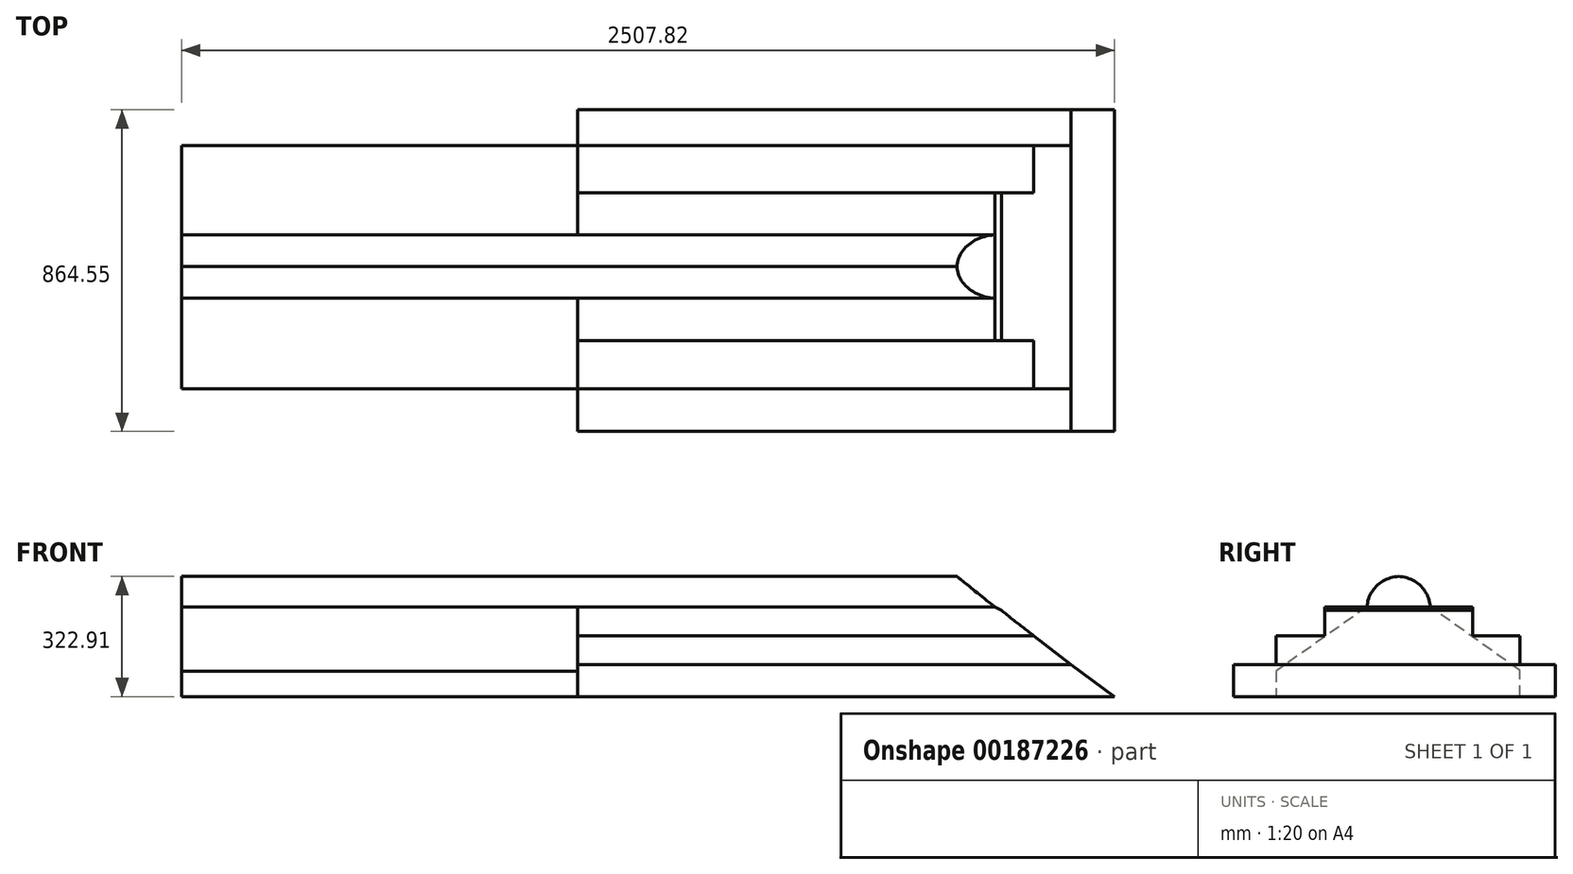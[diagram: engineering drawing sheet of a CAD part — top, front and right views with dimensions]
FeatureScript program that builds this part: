
annotation { "Feature Type Name" : "Feature", "Feature Type Description" : "" }
export const myFeature = defineFeature(function(context is Context, id is Id, definition is map)
    precondition{}
    {
        {
            var Q0;
            Q0=qCreatedBy(makeId("Front.planeOp"),FACE);
            var sketch = newSketch(context, id + "F0", { "sketchPlane" : qUnion([Q0])});
            skLineSegment(sketch, "E0", {"start": v(1047.84, -354.35) * mm, "end": v(909.4, -277.22) * mm});
            skLineSegment(sketch, "E1", {"start": v(909.4, -277.22) * mm, "end": v(-211.95, -277.22) * mm});
            skLineSegment(sketch, "E2", {"start": v(-211.95, -277.22) * mm, "end": v(-211.95, -354.35) * mm});
            skLineSegment(sketch, "E3", {"start": v(-211.95, -354.35) * mm, "end": v(1047.84, -354.35) * mm});
            skSolve(sketch);
        }
        {
            var Q0;
            Q0 = qSketchRegion(id + "F0", true);
            extrude(context, id + "F1", {"entities" : qUnion([Q0]), "oppositeDirection" : true, "depth" : 397.47 * mm});
        }
        {
            var Q0;
            Q0=makeQuery(id+"F1.opExtrude","SWEPT_FACE",FACE,{"disambiguationData":[OSD([sQuery(id+"F0.wireOp",EDGE,"E2")])]});
            var sketch = newSketch(context, id + "F2", { "sketchPlane" : qUnion([Q0])});
            skLineSegment(sketch, "E4", {"start": v(-397.47, -354.35) * mm, "end": v(-524.6, -354.35) * mm});
            skLineSegment(sketch, "E5", {"start": v(-524.6, -354.35) * mm, "end": v(-524.6, -432.67) * mm});
            skLineSegment(sketch, "E6", {"start": v(-524.6, -432.67) * mm, "end": v(130.1, -432.67) * mm});
            skLineSegment(sketch, "E7", {"start": v(130.1, -432.67) * mm, "end": v(130.1, -354.35) * mm});
            skLineSegment(sketch, "E8", {"start": v(130.1, -354.35) * mm, "end": v(0, -354.35) * mm});
            skSolve(sketch);
        }
        {
            var Q0;
            Q0=makeQuery(id+"F2.imprint","IMPRINT",FACE,{"disambiguationData":[TD([[makeQuery(id+"F2.imprint","IMPRINT",EDGE,{"derivedFrom":sQuery(id+"F2.wireOp",EDGE,"E4")}),1.0]])]});
            extrude(context, id + "F3", {"entities" : qUnion([Q0]), "operationType" : NewBodyOperationType.ADD, "oppositeDirection" : true, "depth" : 1384.37 * mm});
        }
        {
            var Q0;
            Q0=makeQuery(id+"F3.opExtrude","CAP_EDGE",EDGE,{"disambiguationData":[OSD([sQuery(id+"F0.wireOp",EDGE,"E2"),sQuery(id+"F0.wireOp",EDGE,"E3"),sQuery(id+"F2.wireOp",EDGE,"E4"),sQuery(id+"F2.wireOp",EDGE,"E8")])],"isStart":false});
            chamfer(context, id + "F4", {"entities" : qUnion([Q0]), "chamferType" : ChamferType.OFFSET_ANGLE, "width" : 124.46 * mm, "oppositeDirection" : false, "angle" : 52 * degree, "tangentPropagation" : true});
        }
        {
            var Q0;
            {var subQ0=sQuery(id+"F0.wireOp",EDGE,"E2");Q0=makeQuery(id+"F3.boolean.opBoolean","MERGE",FACE,{"derivedFrom":[makeQuery(id+"F1.opExtrude","SWEPT_FACE",FACE,{"disambiguationData":[OSD([subQ0])]}),makeQuery(id+"F3.opExtrude","CAP_FACE",FACE,{"disambiguationData":[OSD([subQ0,sQuery(id+"F0.wireOp",EDGE,"E3"),sQuery(id+"F2.wireOp",EDGE,"E4"),sQuery(id+"F2.wireOp",EDGE,"E5"),sQuery(id+"F2.wireOp",EDGE,"E6"),sQuery(id+"F2.wireOp",EDGE,"E7"),sQuery(id+"F2.wireOp",EDGE,"E8")])],"isStart":true})]});}
            var sketch = newSketch(context, id + "F5", { "sketchPlane" : qUnion([Q0])});
            skLineSegment(sketch, "E9.bottom", {"start": v(-620.44, -432.67) * mm, "end": v(244.11, -432.67) * mm});
            skLineSegment(sketch, "E9.top", {"start": v(-620.44, -518.25) * mm, "end": v(244.11, -518.25) * mm});
            skLineSegment(sketch, "E9.left", {"start": v(-620.44, -432.67) * mm, "end": v(-620.44, -518.25) * mm});
            skLineSegment(sketch, "E9.right", {"start": v(244.11, -432.67) * mm, "end": v(244.11, -518.25) * mm});
            skSolve(sketch);
        }
        {
            var Q0;
            Q0 = qSketchRegion(id + "F5", true);
            extrude(context, id + "F6", {"entities" : qUnion([Q0]), "operationType" : NewBodyOperationType.ADD, "oppositeDirection" : true, "depth" : 790.16 * mm});
        }
        {
            var Q0;
            Q0=makeQuery(id+"F6.opExtrude","CAP_FACE",FACE,{"disambiguationData":[OSD([sQuery(id+"F5.wireOp",EDGE,"E9.bottom"),sQuery(id+"F5.wireOp",EDGE,"E9.top"),sQuery(id+"F5.wireOp",EDGE,"E9.left"),sQuery(id+"F5.wireOp",EDGE,"E9.right")])],"isStart":false});
            extrude(context, id + "F7", {"entities" : qUnion([Q0]), "operationType" : NewBodyOperationType.ADD, "depth" : 613 * mm});
        }
        {
            var Q0;
            Q0=makeQuery(id+"F7.opExtrude","CAP_FACE",FACE,{"disambiguationData":[OSD([sQuery(id+"F5.wireOp",EDGE,"E9.bottom"),sQuery(id+"F5.wireOp",EDGE,"E9.top"),sQuery(id+"F5.wireOp",EDGE,"E9.left"),sQuery(id+"F5.wireOp",EDGE,"E9.right")])],"isStart":false});
            extrude(context, id + "F8", {"entities" : qUnion([Q0]), "operationType" : NewBodyOperationType.ADD, "depth" : 11.42 * mm});
        }
        {
            var Q0;
            Q0=makeQuery(id+"F8.opExtrude","CAP_FACE",FACE,{"disambiguationData":[OSD([sQuery(id+"F5.wireOp",EDGE,"E9.bottom"),sQuery(id+"F5.wireOp",EDGE,"E9.top"),sQuery(id+"F5.wireOp",EDGE,"E9.left"),sQuery(id+"F5.wireOp",EDGE,"E9.right")])],"isStart":false});
            extrude(context, id + "F9", {"entities" : qUnion([Q0]), "operationType" : NewBodyOperationType.ADD, "depth" : 29.71 * mm});
        }
        {
            var Q0;
            Q0=makeQuery(id+"F9.opExtrude","CAP_EDGE",EDGE,{"disambiguationData":[OSD([sQuery(id+"F5.wireOp",EDGE,"E9.bottom")])],"isStart":false});
            chamfer(context, id + "F10", {"entities" : qUnion([Q0]), "chamferType" : ChamferType.TWO_OFFSETS, "width1" : 86.36 * mm, "oppositeDirection" : false, "width2" : 118.11 * mm, "tangentPropagation" : true});
        }
        {
            var Q0;
            {var subQ0=sQuery(id+"F0.wireOp",EDGE,"E2");Q0=makeQuery(id+"F6.boolean.opBoolean","MERGE",FACE,{"derivedFrom":[makeQuery(id+"F3.boolean.opBoolean","MERGE",FACE,{"derivedFrom":[makeQuery(id+"F1.opExtrude","SWEPT_FACE",FACE,{"disambiguationData":[OSD([subQ0])]}),makeQuery(id+"F3.opExtrude","CAP_FACE",FACE,{"disambiguationData":[OSD([subQ0,sQuery(id+"F0.wireOp",EDGE,"E3"),sQuery(id+"F2.wireOp",EDGE,"E4"),sQuery(id+"F2.wireOp",EDGE,"E5"),sQuery(id+"F2.wireOp",EDGE,"E6"),sQuery(id+"F2.wireOp",EDGE,"E7"),sQuery(id+"F2.wireOp",EDGE,"E8")])],"isStart":true})]}),makeQuery(id+"F6.opExtrude","CAP_FACE",FACE,{"disambiguationData":[OSD([sQuery(id+"F5.wireOp",EDGE,"E9.bottom"),sQuery(id+"F5.wireOp",EDGE,"E9.top"),sQuery(id+"F5.wireOp",EDGE,"E9.left"),sQuery(id+"F5.wireOp",EDGE,"E9.right")])],"isStart":true})]});}
            var sketch = newSketch(context, id + "F11", { "sketchPlane" : qUnion([Q0])});
            skLineSegment(sketch, "E10.bottom", {"start": v(-284.6, -277.22) * mm, "end": v(-113.72, -277.22) * mm});
            skLineSegment(sketch, "E10.top", {"start": v(-284.6, -195.28) * mm, "end": v(-113.72, -195.28) * mm});
            skLineSegment(sketch, "E10.left", {"start": v(-284.6, -277.22) * mm, "end": v(-284.6, -195.28) * mm});
            skLineSegment(sketch, "E10.right", {"start": v(-113.72, -277.22) * mm, "end": v(-113.72, -195.28) * mm});
            skSolve(sketch);
        }
        {
            var Q0;
            Q0 = qSketchRegion(id + "F11", true);
            extrude(context, id + "F12", {"entities" : qUnion([Q0]), "operationType" : NewBodyOperationType.ADD, "oppositeDirection" : true, "depth" : 1120.73 * mm});
        }
        {
            var Q0;
            Q0=makeQuery(id+"F12.opExtrude","CAP_EDGE",EDGE,{"disambiguationData":[OSD([sQuery(id+"F11.wireOp",EDGE,"E10.top")])],"isStart":false});
            chamfer(context, id + "F13", {"entities" : qUnion([Q0]), "chamferType" : ChamferType.TWO_OFFSETS, "width1" : 81.8 * mm, "oppositeDirection" : false, "width2" : 101.6 * mm, "tangentPropagation" : true});
        }
        {
            var Q0;
            Q0=makeQuery(id+"F12.opExtrude","SWEPT_EDGE",EDGE,{"disambiguationData":[OSD([sQuery(id+"F11.wireOp",EDGE,"E10.top"),sQuery(id+"F11.wireOp",EDGE,"E10.left")])]});
            var Q1;
            Q1=makeQuery(id+"F12.opExtrude","SWEPT_EDGE",EDGE,{"disambiguationData":[OSD([sQuery(id+"F11.wireOp",EDGE,"E10.top"),sQuery(id+"F11.wireOp",EDGE,"E10.right")])]});
            fillet(context, id + "F14", {"entities" : qUnion([Q0, Q1]), "radius" : 88.9 * mm, "tangentPropagation" : true, "allowEdgeOverflow" : false});
        }
        {
            var Q0;
            {var subQ0=sQuery(id+"F0.wireOp",EDGE,"E2");Q0=makeQuery(id+"F12.boolean.opBoolean","MERGE",FACE,{"derivedFrom":[makeQuery(id+"F6.boolean.opBoolean","MERGE",FACE,{"derivedFrom":[makeQuery(id+"F3.boolean.opBoolean","MERGE",FACE,{"derivedFrom":[makeQuery(id+"F1.opExtrude","SWEPT_FACE",FACE,{"disambiguationData":[OSD([subQ0])]}),makeQuery(id+"F3.opExtrude","CAP_FACE",FACE,{"disambiguationData":[OSD([subQ0,sQuery(id+"F0.wireOp",EDGE,"E3"),sQuery(id+"F2.wireOp",EDGE,"E4"),sQuery(id+"F2.wireOp",EDGE,"E5"),sQuery(id+"F2.wireOp",EDGE,"E6"),sQuery(id+"F2.wireOp",EDGE,"E7"),sQuery(id+"F2.wireOp",EDGE,"E8")])],"isStart":true})]}),makeQuery(id+"F6.opExtrude","CAP_FACE",FACE,{"disambiguationData":[OSD([sQuery(id+"F5.wireOp",EDGE,"E9.bottom"),sQuery(id+"F5.wireOp",EDGE,"E9.top"),sQuery(id+"F5.wireOp",EDGE,"E9.left"),sQuery(id+"F5.wireOp",EDGE,"E9.right")])],"isStart":true})]}),makeQuery(id+"F12.opExtrude","CAP_FACE",FACE,{"disambiguationData":[OSD([sQuery(id+"F11.wireOp",EDGE,"E10.bottom"),sQuery(id+"F11.wireOp",EDGE,"E10.top"),sQuery(id+"F11.wireOp",EDGE,"E10.left"),sQuery(id+"F11.wireOp",EDGE,"E10.right")])],"isStart":true})]});}
            var sketch = newSketch(context, id + "F15", { "sketchPlane" : qUnion([Q0])});
            skLineSegment(sketch, "E11", {"start": v(-524.6, -518.25) * mm, "end": v(-524.6, -448.06) * mm});
            skLineSegment(sketch, "E12", {"start": v(-524.6, -448.06) * mm, "end": v(-284.6, -277.22) * mm});
            skLineSegment(sketch, "E13", {"start": v(-284.6, -277.22) * mm, "end": v(-113.72, -277.22) * mm});
            skLineSegment(sketch, "E14", {"start": v(-113.72, -277.22) * mm, "end": v(130.1, -449.86) * mm});
            skLineSegment(sketch, "E15", {"start": v(130.1, -449.86) * mm, "end": v(130.1, -518.25) * mm});
            skLineSegment(sketch, "E16", {"start": v(130.1, -518.25) * mm, "end": v(-524.6, -518.25) * mm});
            skSolve(sketch);
        }
        {
            var Q0;
            Q0 = qSketchRegion(id + "F15", true);
            extrude(context, id + "F16", {"entities" : qUnion([Q0]), "operationType" : NewBodyOperationType.ADD, "depth" : 1064.6 * mm});
        }
        {
            var Q0;
            Q0=makeQuery(id+"F16.opExtrude","CAP_FACE",FACE,{"disambiguationData":[OSD([sQuery(id+"F15.wireOp",EDGE,"E11"),sQuery(id+"F15.wireOp",EDGE,"E12"),sQuery(id+"F15.wireOp",EDGE,"E13"),sQuery(id+"F15.wireOp",EDGE,"E14"),sQuery(id+"F15.wireOp",EDGE,"E15"),sQuery(id+"F15.wireOp",EDGE,"E16")])],"isStart":false});
            extrude(context, id + "F17", {"entities" : qUnion([Q0]), "operationType" : NewBodyOperationType.ADD, "oppositeDirection" : true, "depth" : 77.8 * mm});
        }
        {
            var Q0;
            {var subQ0=makeQuery(id+"F6.opExtrude","CAP_FACE",FACE,{"disambiguationData":[OSD([sQuery(id+"F5.wireOp",EDGE,"E9.bottom"),sQuery(id+"F5.wireOp",EDGE,"E9.top"),sQuery(id+"F5.wireOp",EDGE,"E9.left"),sQuery(id+"F5.wireOp",EDGE,"E9.right")])],"isStart":true});var subQ1=sQuery(id+"F0.wireOp",EDGE,"E2");var subQ2=makeQuery(id+"F3.opExtrude","CAP_FACE",FACE,{"disambiguationData":[OSD([subQ1,sQuery(id+"F0.wireOp",EDGE,"E3"),sQuery(id+"F2.wireOp",EDGE,"E4"),sQuery(id+"F2.wireOp",EDGE,"E5"),sQuery(id+"F2.wireOp",EDGE,"E6"),sQuery(id+"F2.wireOp",EDGE,"E7"),sQuery(id+"F2.wireOp",EDGE,"E8")])],"isStart":true});var subQ3=makeQuery(id+"F1.opExtrude","SWEPT_FACE",FACE,{"disambiguationData":[OSD([subQ1])]});var subQ4=sQuery(id+"F11.wireOp",EDGE,"E10.right");var subQ5=sQuery(id+"F11.wireOp",EDGE,"E10.left");var subQ6=sQuery(id+"F11.wireOp",EDGE,"E10.top");var subQ7=makeQuery(id+"F12.opExtrude","CAP_FACE",FACE,{"disambiguationData":[OSD([sQuery(id+"F11.wireOp",EDGE,"E10.bottom"),subQ6,subQ5,subQ4])],"isStart":true});Q0=makeQuery(id+"F16.boolean.opBoolean","SPLIT",FACE,{"disambiguationData":[TD([makeQuery(id+"F1.opExtrude","SWEPT_FACE",FACE,{"disambiguationData":[OSD([sQuery(id+"F0.wireOp",EDGE,"E1")])]}),subQ3,subQ2,subQ0,subQ7,makeQuery(id+"F14.opFillet","BLEND_FACE",FACE,{"disambiguationData":[OSD([subQ6,subQ5])]}),makeQuery(id+"F14.opFillet","BLEND_FACE",FACE,{"disambiguationData":[OSD([subQ6,subQ4])]}),makeQuery(id+"F16.opExtrude","SWEPT_FACE",FACE,{"disambiguationData":[OSD([sQuery(id+"F15.wireOp",EDGE,"E12")])]}),makeQuery(id+"F16.opExtrude","SWEPT_FACE",FACE,{"disambiguationData":[OSD([sQuery(id+"F15.wireOp",EDGE,"E13")])]}),makeQuery(id+"F16.opExtrude","SWEPT_FACE",FACE,{"disambiguationData":[OSD([sQuery(id+"F15.wireOp",EDGE,"E14")])]})])],"derivedFrom":makeQuery(id+"F12.boolean.opBoolean","MERGE",FACE,{"derivedFrom":[makeQuery(id+"F6.boolean.opBoolean","MERGE",FACE,{"derivedFrom":[makeQuery(id+"F3.boolean.opBoolean","MERGE",FACE,{"derivedFrom":[subQ3,subQ2]}),subQ0]}),subQ7]})});}
            extrude(context, id + "F18", {"entities" : qUnion([Q0]), "operationType" : NewBodyOperationType.ADD, "depth" : 1025.7 * mm});
        }
        {
            var Q0;
            Q0=makeQuery(id+"F18.opExtrude","CAP_FACE",FACE,{"disambiguationData":[OSD([sQuery(id+"F0.wireOp",EDGE,"E2"),sQuery(id+"F0.wireOp",EDGE,"E3"),sQuery(id+"F2.wireOp",EDGE,"E4"),sQuery(id+"F2.wireOp",EDGE,"E5"),sQuery(id+"F2.wireOp",EDGE,"E6"),sQuery(id+"F2.wireOp",EDGE,"E7"),sQuery(id+"F2.wireOp",EDGE,"E8"),sQuery(id+"F5.wireOp",EDGE,"E9.bottom"),sQuery(id+"F5.wireOp",EDGE,"E9.top"),sQuery(id+"F5.wireOp",EDGE,"E9.left"),sQuery(id+"F5.wireOp",EDGE,"E9.right"),sQuery(id+"F11.wireOp",EDGE,"E10.bottom"),sQuery(id+"F11.wireOp",EDGE,"E10.top"),sQuery(id+"F11.wireOp",EDGE,"E10.left"),sQuery(id+"F11.wireOp",EDGE,"E10.right")])],"isStart":false});
            extrude(context, id + "F19", {"entities" : qUnion([Q0]), "operationType" : NewBodyOperationType.ADD, "depth" : 38.06 * mm});
        }
    });
